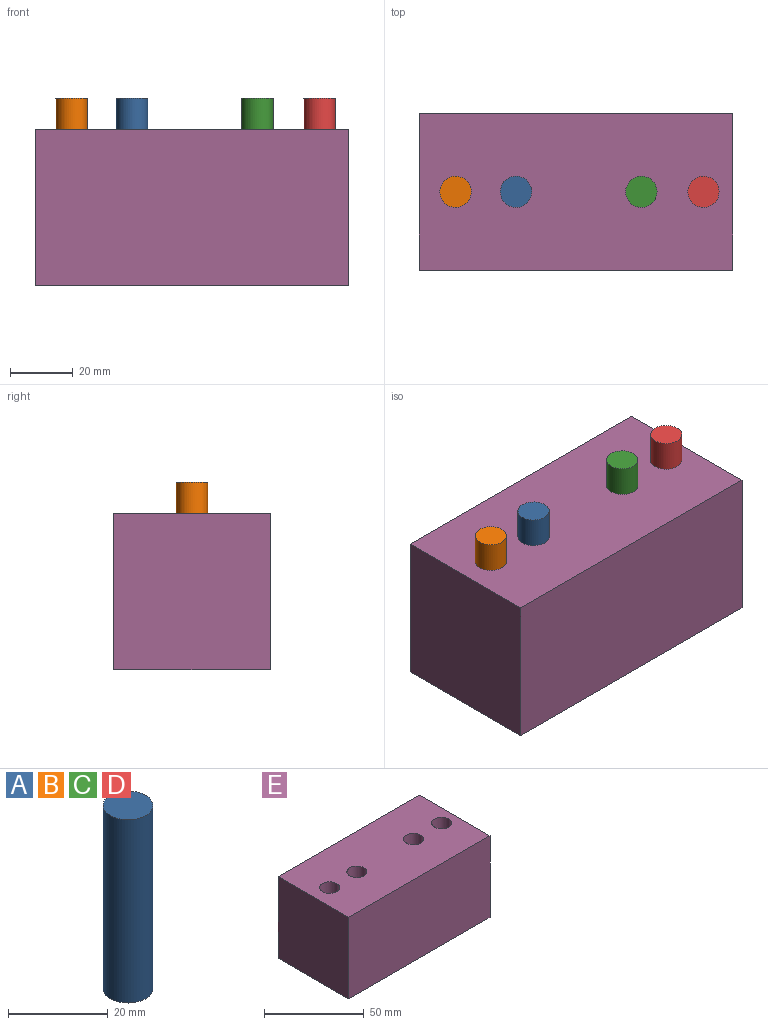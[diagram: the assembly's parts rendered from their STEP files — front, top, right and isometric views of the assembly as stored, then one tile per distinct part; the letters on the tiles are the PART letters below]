
ASSEMBLY  parts=5 mates=4
PART A: 3 faces, bbox 10x10x45 mm
  f0: cylinder r=5mm len=45mm, axis (0,0,-1), area 1413.7mm2, adj f1,f2
  f1: plane 10x10mm, normal (0,0,1), area 78.5mm2, adj f0
  f2: plane 10x10mm, normal (0,0,-1), area 78.5mm2, adj f0
PART B: same geometry as A
PART C: same geometry as A
PART D: same geometry as A
PART E: 14 faces, bbox 100x50x50 mm
  f0: plane 50x50mm, normal (-1,0,0), area 2500mm2, adj f1,f3,f4,f5
  f1: plane 100x50mm, normal (0,-1,0), area 5000mm2, adj f0,f2,f4,f5
  f2: plane 50x50mm, normal (1,0,0), area 2500mm2, adj f1,f3,f4,f5
  f3: plane 100x50mm, normal (0,1,0), area 5000mm2, adj f0,f2,f4,f5
  f4: plane 100x50mm, normal (0,0,1), area 4685.8mm2, adj f0,f1,f2,f3,f6,f8,f10,f12
  f5: plane 100x50mm, normal (0,0,-1), area 5000mm2, adj f0,f1,f2,f3
  f6: cylinder r=5mm len=45mm, axis (0,0,1), area 1413.7mm2, adj f4,f7
  f7: plane 10x10mm, normal (0,0,1), area 78.5mm2, adj f6
  f8: cylinder r=5mm len=45mm, axis (0,0,1), area 1413.7mm2, adj f4,f9
  f9: plane 10x10mm, normal (0,0,1), area 78.5mm2, adj f8
  f10: cylinder r=5mm len=45mm, axis (0,0,1), area 1413.7mm2, adj f4,f11
  f11: plane 10x10mm, normal (0,0,1), area 78.5mm2, adj f10
  f12: cylinder r=5mm len=45mm, axis (0,0,1), area 1413.7mm2, adj f4,f13
  f13: plane 10x10mm, normal (0,0,1), area 78.5mm2, adj f12
PLACE A t=(-19.15,0,37.5)mm
PLACE B t=(-38.5,0,37.5)mm
PLACE C rot(axis=(1,0,0),0deg) t=(20.88,0,37.5)mm
PLACE D t=(40.72,0,37.5)mm
PLACE E at identity fixed
MATE slider C.f0 <-> E.f8  axis (0,0,-1) through (20.88,0,15)mm
MATE slider B.f0 <-> E.f12  axis (0,0,-1) through (-38.5,0,15)mm
MATE slider E.f6 <-> D.f0  axis (0,0,1) through (40.72,0,50)mm
MATE slider A.f0 <-> E.f10  axis (0,0,-1) through (-19.15,0,15)mm
